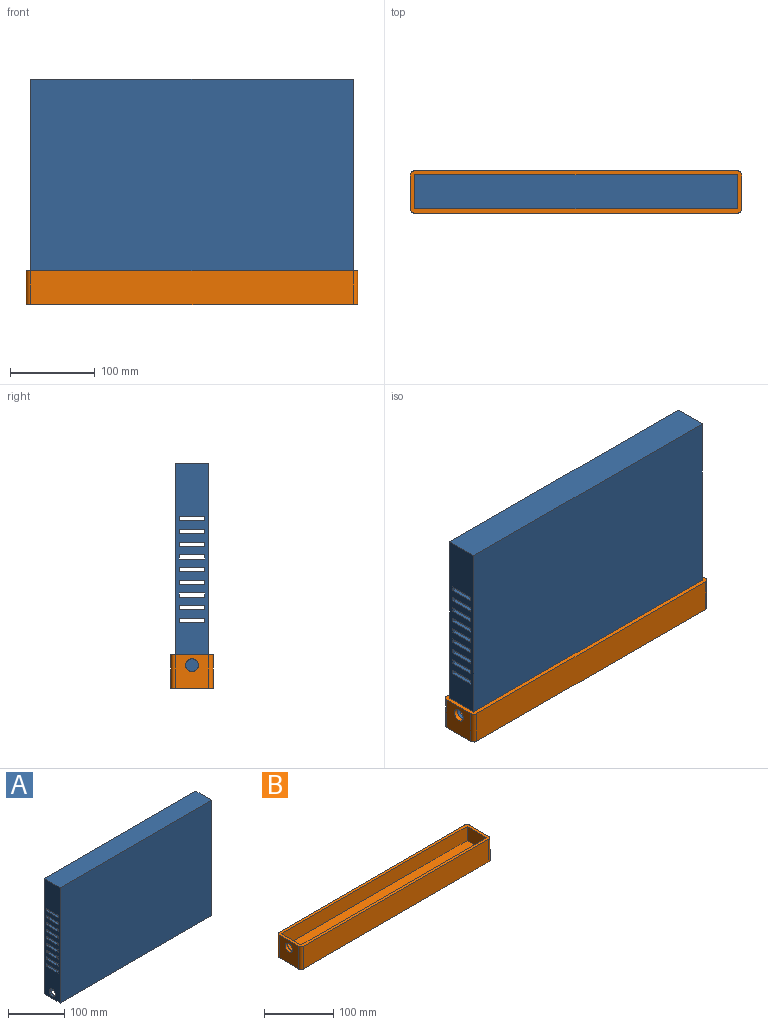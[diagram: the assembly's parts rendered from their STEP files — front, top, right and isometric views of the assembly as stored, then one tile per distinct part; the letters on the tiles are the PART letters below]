
ASSEMBLY  parts=2 mates=1
PART A: 84 faces, bbox 380x40x250 mm
  f0: plane 250x40mm, normal (-1,0,0), area 8473.3mm2, adj f4,f5,f6,f7,f47,f48,f49,f50
  f1: plane 250x40mm, normal (1,0,0), area 8650mm2, adj f4,f5,f6,f7,f11,f12,f13,f14
  f2: plane 246x32mm, normal (1,0,0), area 6345.3mm2, adj f4,f8,f9,f10,f47,f48,f49,f50
  f3: plane 246x32mm, normal (-1,0,0), area 6522mm2, adj f4,f8,f9,f10,f11,f12,f13,f14
  f4: plane 380x40mm, normal (0,0,-1), area 3296mm2, adj f0,f1,f2,f3,f5,f6,f8,f9
  f5: plane 380x250mm, normal (0,1,0), area 95000mm2, adj f0,f1,f4,f7
  f6: plane 380x250mm, normal (0,-1,0), area 95000mm2, adj f0,f1,f4,f7
  f7: plane 380x40mm, normal (0,0,1), area 15200mm2, adj f0,f1,f5,f6
  f8: plane 372x246mm, normal (0,-1,0), area 91512mm2, adj f2,f3,f4,f10
  f9: plane 372x246mm, normal (0,1,0), area 91512mm2, adj f2,f3,f4,f10
  f10: plane 372x32mm, normal (0,0,-1), area 11904mm2, adj f2,f3,f8,f9
  f11: plane 5x4mm, normal (0,1,0), area 20mm2, adj f1,f3,f12,f14
  f12: plane 30x4mm, normal (0,0,1), area 120mm2, adj f1,f3,f11,f13
  f13: plane 5x4mm, normal (0,-1,0), area 20mm2, adj f1,f3,f12,f14
  f14: plane 30x4mm, normal (0,0,-1), area 120mm2, adj f1,f3,f11,f13
  f15: plane 5x4mm, normal (0,1,0), area 20mm2, adj f1,f3,f16,f18
  f16: plane 30x4mm, normal (0,0,1), area 120mm2, adj f1,f3,f15,f17
  f17: plane 5x4mm, normal (0,-1,0), area 20mm2, adj f1,f3,f16,f18
  f18: plane 30x4mm, normal (0,0,-1), area 120mm2, adj f1,f3,f15,f17
  f19: plane 5x4mm, normal (0,1,0), area 20mm2, adj f1,f3,f20,f22
  f20: plane 30x4mm, normal (0,0,1), area 120mm2, adj f1,f3,f19,f21
  f21: plane 5x4mm, normal (0,-1,0), area 20mm2, adj f1,f3,f20,f22
  f22: plane 30x4mm, normal (0,0,-1), area 120mm2, adj f1,f3,f19,f21
  f23: plane 5x4mm, normal (0,1,0), area 20mm2, adj f1,f3,f24,f26
  f24: plane 30x4mm, normal (0,0,1), area 120mm2, adj f1,f3,f23,f25
  f25: plane 5x4mm, normal (0,-1,0), area 20mm2, adj f1,f3,f24,f26
  f26: plane 30x4mm, normal (0,0,-1), area 120mm2, adj f1,f3,f23,f25
  f27: plane 5x4mm, normal (0,1,0), area 20mm2, adj f1,f3,f28,f30
  f28: plane 30x4mm, normal (0,0,1), area 120mm2, adj f1,f3,f27,f29
  f29: plane 5x4mm, normal (0,-1,0), area 20mm2, adj f1,f3,f28,f30
  f30: plane 30x4mm, normal (0,0,-1), area 120mm2, adj f1,f3,f27,f29
  f31: plane 5x4mm, normal (0,1,0), area 20mm2, adj f1,f3,f32,f34
  f32: plane 30x4mm, normal (0,0,1), area 120mm2, adj f1,f3,f31,f33
  f33: plane 5x4mm, normal (0,-1,0), area 20mm2, adj f1,f3,f32,f34
  f34: plane 30x4mm, normal (0,0,-1), area 120mm2, adj f1,f3,f31,f33
  f35: plane 5x4mm, normal (0,1,0), area 20mm2, adj f1,f3,f36,f38
  f36: plane 30x4mm, normal (0,0,1), area 120mm2, adj f1,f3,f35,f37
  f37: plane 5x4mm, normal (0,-1,0), area 20mm2, adj f1,f3,f36,f38
  f38: plane 30x4mm, normal (0,0,-1), area 120mm2, adj f1,f3,f35,f37
  f39: plane 5x4mm, normal (0,1,0), area 20mm2, adj f1,f3,f40,f42
  f40: plane 30x4mm, normal (0,0,1), area 120mm2, adj f1,f3,f39,f41
  f41: plane 5x4mm, normal (0,-1,0), area 20mm2, adj f1,f3,f40,f42
  f42: plane 30x4mm, normal (0,0,-1), area 120mm2, adj f1,f3,f39,f41
  f43: plane 5x4mm, normal (0,1,0), area 20mm2, adj f1,f3,f44,f46
  f44: plane 30x4mm, normal (0,0,1), area 120mm2, adj f1,f3,f43,f45
  f45: plane 5x4mm, normal (0,-1,0), area 20mm2, adj f1,f3,f44,f46
  f46: plane 30x4mm, normal (0,0,-1), area 120mm2, adj f1,f3,f43,f45
  f47: plane 30x4mm, normal (0,0,-1), area 120mm2, adj f0,f2,f48,f50
  f48: plane 5x4mm, normal (0,-1,0), area 20mm2, adj f0,f2,f47,f49
  f49: plane 30x4mm, normal (0,0,1), area 120mm2, adj f0,f2,f48,f50
  f50: plane 5x4mm, normal (0,1,0), area 20mm2, adj f0,f2,f47,f49
  f51: plane 30x4mm, normal (0,0,-1), area 120mm2, adj f0,f2,f52,f54
  f52: plane 5x4mm, normal (0,-1,0), area 20mm2, adj f0,f2,f51,f53
  f53: plane 30x4mm, normal (0,0,1), area 120mm2, adj f0,f2,f52,f54
  f54: plane 5x4mm, normal (0,1,0), area 20mm2, adj f0,f2,f51,f53
  f55: plane 30x4mm, normal (0,0,-1), area 120mm2, adj f0,f2,f56,f58
  f56: plane 5x4mm, normal (0,-1,0), area 20mm2, adj f0,f2,f55,f57
  f57: plane 30x4mm, normal (0,0,1), area 120mm2, adj f0,f2,f56,f58
  f58: plane 5x4mm, normal (0,1,0), area 20mm2, adj f0,f2,f55,f57
  f59: plane 30x4mm, normal (0,0,-1), area 120mm2, adj f0,f2,f60,f62
  f60: plane 5x4mm, normal (0,-1,0), area 20mm2, adj f0,f2,f59,f61
  f61: plane 30x4mm, normal (0,0,1), area 120mm2, adj f0,f2,f60,f62
  f62: plane 5x4mm, normal (0,1,0), area 20mm2, adj f0,f2,f59,f61
  f63: plane 30x4mm, normal (0,0,-1), area 120mm2, adj f0,f2,f64,f66
  f64: plane 5x4mm, normal (0,-1,0), area 20mm2, adj f0,f2,f63,f65
  f65: plane 30x4mm, normal (0,0,1), area 120mm2, adj f0,f2,f64,f66
  f66: plane 5x4mm, normal (0,1,0), area 20mm2, adj f0,f2,f63,f65
  f67: plane 30x4mm, normal (0,0,-1), area 120mm2, adj f0,f2,f68,f70
  f68: plane 5x4mm, normal (0,-1,0), area 20mm2, adj f0,f2,f67,f69
  f69: plane 30x4mm, normal (0,0,1), area 120mm2, adj f0,f2,f68,f70
  f70: plane 5x4mm, normal (0,1,0), area 20mm2, adj f0,f2,f67,f69
  f71: plane 30x4mm, normal (0,0,-1), area 120mm2, adj f0,f2,f72,f74
  f72: plane 5x4mm, normal (0,-1,0), area 20mm2, adj f0,f2,f71,f73
  f73: plane 30x4mm, normal (0,0,1), area 120mm2, adj f0,f2,f72,f74
  f74: plane 5x4mm, normal (0,1,0), area 20mm2, adj f0,f2,f71,f73
  f75: plane 30x4mm, normal (0,0,-1), area 120mm2, adj f0,f2,f76,f78
  f76: plane 5x4mm, normal (0,-1,0), area 20mm2, adj f0,f2,f75,f77
  f77: plane 30x4mm, normal (0,0,1), area 120mm2, adj f0,f2,f76,f78
  f78: plane 5x4mm, normal (0,1,0), area 20mm2, adj f0,f2,f75,f77
  f79: plane 30x4mm, normal (0,0,-1), area 120mm2, adj f0,f2,f80,f82
  f80: plane 5x4mm, normal (0,-1,0), area 20mm2, adj f0,f2,f79,f81
  f81: plane 30x4mm, normal (0,0,1), area 120mm2, adj f0,f2,f80,f82
  f82: plane 5x4mm, normal (0,1,0), area 20mm2, adj f0,f2,f79,f81
  f83: cylinder r=7.5mm len=15mm, axis (-1,0,0), area 188.5mm2, adj f0,f2
PART B: 16 faces, bbox 390x50x40 mm
  f0: plane 390x50mm, normal (0,0,1), area 4278.5mm2, adj f1,f2,f3,f4,f6,f7,f8,f9
  f1: plane 380x40mm, normal (0,1,0), area 15200mm2, adj f0,f5,f11,f14
  f2: plane 40x40mm, normal (-1,0,0), area 1423.3mm2, adj f0,f5,f11,f12,f15
  f3: plane 380x40mm, normal (0,-1,0), area 15200mm2, adj f0,f5,f12,f13
  f4: plane 40x40mm, normal (1,0,0), area 1600mm2, adj f0,f5,f13,f14
  f5: plane 390x50mm, normal (0,0,-1), area 19478.5mm2, adj f1,f2,f3,f4,f11,f12,f13,f14
  f6: plane 380x25mm, normal (0,-1,0), area 9500mm2, adj f0,f7,f9,f10
  f7: plane 40x25mm, normal (1,0,0), area 823.3mm2, adj f0,f6,f8,f10,f15
  f8: plane 380x25mm, normal (0,1,0), area 9500mm2, adj f0,f7,f9,f10
  f9: plane 40x25mm, normal (-1,0,0), area 1000mm2, adj f0,f6,f8,f10
  f10: plane 380x40mm, normal (0,0,1), area 15200mm2, adj f6,f7,f8,f9
  f11: cylinder r=5mm len=40mm, axis (0,0,1), area 314.2mm2, adj f0,f1,f2,f5
  f12: cylinder r=5mm len=40mm, axis (0,0,-1), area 314.2mm2, adj f0,f2,f3,f5
  f13: cylinder r=5mm len=40mm, axis (0,0,1), area 314.2mm2, adj f0,f3,f4,f5
  f14: cylinder r=5mm len=40mm, axis (0,0,-1), area 314.2mm2, adj f0,f1,f4,f5
  f15: cylinder r=7.5mm len=15mm, axis (1,0,0), area 235.6mm2, adj f2,f7
PLACE A t=(-161.6,6.64,-5.54)mm
PLACE B t=(-161.6,6.64,-20.54)mm
MATE slider B.f12 <-> A.f4  axis (0,0,1) through (-351.6,-13.36,-5.54)mm
